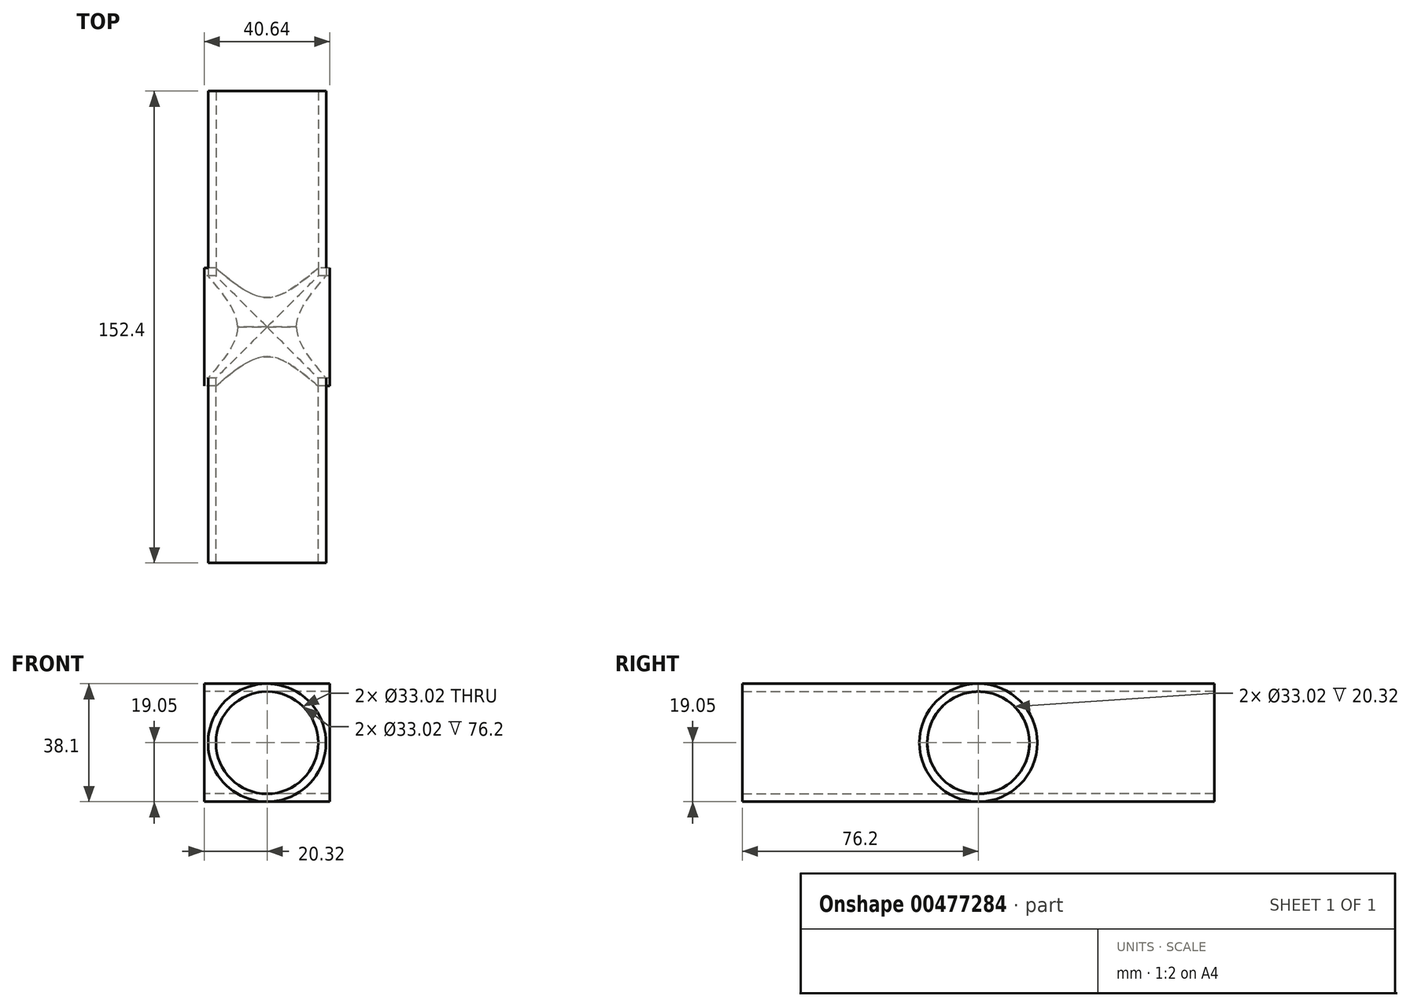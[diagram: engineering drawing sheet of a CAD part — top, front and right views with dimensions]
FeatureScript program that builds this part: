
annotation { "Feature Type Name" : "Feature", "Feature Type Description" : "" }
export const myFeature = defineFeature(function(context is Context, id is Id, definition is map)
    precondition{}
    {
        {
            var Q0;
            Q0=qCreatedBy(makeId("Front.planeOp"),FACE);
            var sketch = newSketch(context, id + "F0", { "sketchPlane" : qUnion([Q0])});
            skCircle(sketch, "E0", {"center": v(0, 0) * mm, "radius": 19.05 * mm});
            skSolve(sketch);
        }
        {
            var Q0;
            Q0=makeQuery(id+"F0.imprint","IMPRINT",FACE,{"disambiguationData":[TD([[makeQuery(id+"F0.imprint","IMPRINT",EDGE,{"derivedFrom":sQuery(id+"F0.wireOp",EDGE,"E0")}),1.0]])]});
            extrude(context, id + "F1", {"entities" : qUnion([Q0]), "depth" : 76.2 * mm});
        }
        {
            var Q0;
            Q0=qCreatedBy(makeId("Right.planeOp"),FACE);
            var sketch = newSketch(context, id + "F2", { "sketchPlane" : qUnion([Q0])});
            skCircle(sketch, "E1", {"center": v(0, 0) * mm, "radius": 19.05 * mm});
            skSolve(sketch);
        }
        {
            var Q0;
            Q0=makeQuery(id+"F2.imprint","IMPRINT",FACE,{"disambiguationData":[TD([[makeQuery(id+"F2.imprint","IMPRINT",EDGE,{"derivedFrom":sQuery(id+"F2.wireOp",EDGE,"E1")}),1.0]])]});
            extrude(context, id + "F3", {"entities" : qUnion([Q0]), "endBound" : BoundingType.SYMMETRIC, "depth" : 40.64 * mm});
        }
        {
            var Q0;
            Q0 = qSketchRegion(id + "F0", true);
            var Q1;
            Q1=sQuery(id+"F0.wireOp",EDGE,"E0");
            extrude(context, id + "F4", {"entities" : qUnion([Q0]), "surfaceEntities" : qUnion([Q1]), "oppositeDirection" : true, "depth" : 76.2 * mm});
        }
        {
            var Q0;
            Q0=sQuery(id+"F2.wireOp",VERTEX,"E1.center");
            var Q1;
            Q1=makeQuery(id+"F1.opExtrude","SWEPT_BODY",BODY,{"disambiguationData":[OSD([sQuery(id+"F0.wireOp",EDGE,"E0")])]});
            var Q2;
            Q2=makeQuery(id+"F3.opExtrude","SWEPT_BODY",BODY,{"disambiguationData":[OSD([sQuery(id+"F2.wireOp",EDGE,"E1")])]});
            var Q3;
            Q3=makeQuery(id+"F4.opExtrude","SWEPT_BODY",BODY,{"disambiguationData":[OSD([sQuery(id+"F0.wireOp",EDGE,"E0")])]});
            hole(context, id + "F5", {"style" : HoleStyle.SIMPLE, "endStyle" : HoleEndStyle.THROUGH, "oppositeDirection" : true, "holeDiameter" : 33.02 * mm, "isTappedThrough" : true, "tappedDepth" : 12.7 * mm, "tapClearance" : 3, "startFromSketch" : true, "locations" : qUnion([Q0]), "scope" : qUnion([Q1, Q2, Q3])});
        }
        {
            var Q0;
            Q0=sQuery(id+"F2.wireOp",VERTEX,"E1.center");
            var Q1;
            Q1=makeQuery(id+"F1.opExtrude","SWEPT_BODY",BODY,{"disambiguationData":[OSD([sQuery(id+"F0.wireOp",EDGE,"E0")])]});
            var Q2;
            Q2=makeQuery(id+"F3.opExtrude","SWEPT_BODY",BODY,{"disambiguationData":[OSD([sQuery(id+"F2.wireOp",EDGE,"E1")])]});
            var Q3;
            Q3=makeQuery(id+"F4.opExtrude","SWEPT_BODY",BODY,{"disambiguationData":[OSD([sQuery(id+"F0.wireOp",EDGE,"E0")])]});
            hole(context, id + "F6", {"style" : HoleStyle.SIMPLE, "endStyle" : HoleEndStyle.THROUGH, "holeDiameter" : 33.02 * mm, "isTappedThrough" : true, "tappedDepth" : 12.7 * mm, "tapClearance" : 3, "startFromSketch" : true, "locations" : qUnion([Q0]), "scope" : qUnion([Q1, Q2, Q3])});
        }
        {
            var Q0;
            Q0=sQuery(id+"F0.wireOp",VERTEX,"E0.center");
            var Q1;
            Q1=makeQuery(id+"F3.opExtrude","SWEPT_BODY",BODY,{"disambiguationData":[OSD([sQuery(id+"F2.wireOp",EDGE,"E1")])]});
            var Q2;
            Q2=makeQuery(id+"F1.opExtrude","SWEPT_BODY",BODY,{"disambiguationData":[OSD([sQuery(id+"F0.wireOp",EDGE,"E0")])]});
            hole(context, id + "F7", {"style" : HoleStyle.SIMPLE, "endStyle" : HoleEndStyle.THROUGH, "oppositeDirection" : true, "holeDiameter" : 33.02 * mm, "isTappedThrough" : true, "tappedDepth" : 12.7 * mm, "tapClearance" : 3, "locations" : qUnion([Q0]), "scope" : qUnion([Q1, Q2])});
        }
        {
            var Q0;
            Q0=sQuery(id+"F0.wireOp",VERTEX,"E0.center");
            var Q1;
            Q1=makeQuery(id+"F4.opExtrude","SWEPT_BODY",BODY,{"disambiguationData":[OSD([sQuery(id+"F0.wireOp",EDGE,"E0")])]});
            var Q2;
            Q2=makeQuery(id+"F3.opExtrude","SWEPT_BODY",BODY,{"disambiguationData":[OSD([sQuery(id+"F2.wireOp",EDGE,"E1")])]});
            hole(context, id + "F8", {"style" : HoleStyle.SIMPLE, "endStyle" : HoleEndStyle.THROUGH, "holeDiameter" : 33.02 * mm, "isTappedThrough" : true, "tappedDepth" : 12.7 * mm, "tapClearance" : 3, "locations" : qUnion([Q0]), "scope" : qUnion([Q1, Q2])});
        }
    });
